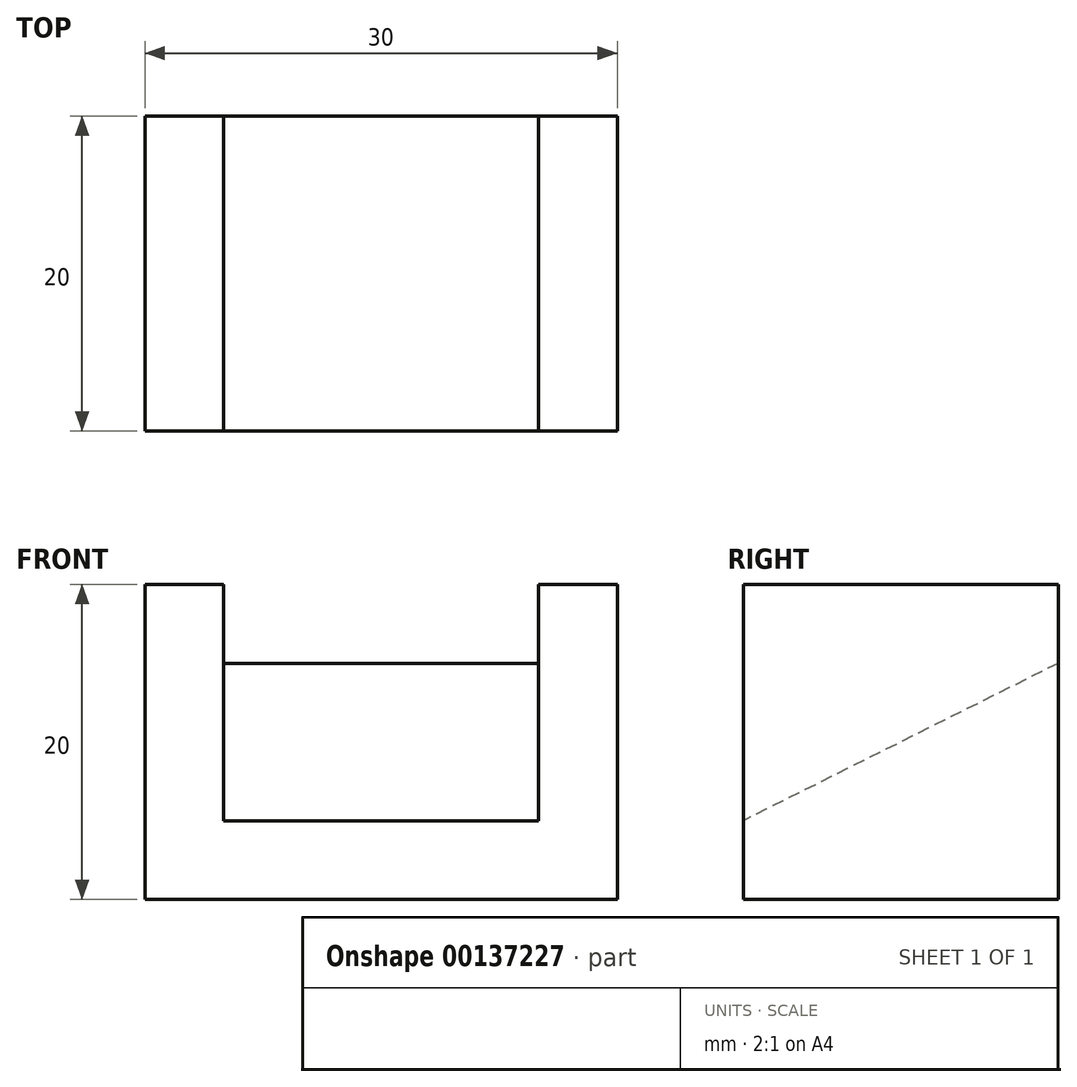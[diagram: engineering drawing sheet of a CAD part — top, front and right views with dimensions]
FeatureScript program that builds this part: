
annotation { "Feature Type Name" : "Feature", "Feature Type Description" : "" }
export const myFeature = defineFeature(function(context is Context, id is Id, definition is map)
    precondition{}
    {
        {
            var Q0;
            Q0=qCreatedBy(makeId("Front.planeOp"),FACE);
            var sketch = newSketch(context, id + "F0", { "sketchPlane" : qUnion([Q0])});
            skLineSegment(sketch, "E0", {"start": v(0, 0) * mm, "end": v(30, 0) * mm});
            skLineSegment(sketch, "E1", {"start": v(30, 0) * mm, "end": v(30, 20) * mm});
            skLineSegment(sketch, "E2", {"start": v(30, 20) * mm, "end": v(25, 20) * mm});
            skLineSegment(sketch, "E3", {"start": v(25, 20) * mm, "end": v(25, 5) * mm});
            skLineSegment(sketch, "E4", {"start": v(25, 5) * mm, "end": v(5, 5) * mm});
            skLineSegment(sketch, "E5", {"start": v(5, 5) * mm, "end": v(5, 20) * mm});
            skLineSegment(sketch, "E6", {"start": v(5, 20) * mm, "end": v(0, 20) * mm});
            skLineSegment(sketch, "E7", {"start": v(0, 20) * mm, "end": v(0, 0) * mm});
            skSolve(sketch);
        }
        {
            var Q0;
            Q0=makeQuery(id+"F0.imprint","IMPRINT",FACE,{"disambiguationData":[TD([[makeQuery(id+"F0.imprint","IMPRINT",EDGE,{"derivedFrom":sQuery(id+"F0.wireOp",EDGE,"E0")}),1.0]])]});
            extrude(context, id + "F1", {"entities" : qUnion([Q0]), "oppositeDirection" : true, "depth" : 20 * mm});
        }
        {
            var Q0;
            Q0=makeQuery(id+"F1.opExtrude","SWEPT_FACE",FACE,{"disambiguationData":[OSD([sQuery(id+"F0.wireOp",EDGE,"E5")])]});
            var sketch = newSketch(context, id + "F2", { "sketchPlane" : qUnion([Q0])});
            skLineSegment(sketch, "E8", {"start": v(20, 20) * mm, "end": v(20, 15) * mm, "construction": true});
            skLineSegment(sketch, "E9", {"start": v(20, 15) * mm, "end": v(0, 5) * mm});
            skLineSegment(sketch, "E10", {"start": v(0, 5) * mm, "end": v(20, 5) * mm});
            skLineSegment(sketch, "E11", {"start": v(20, 5) * mm, "end": v(20, 15) * mm});
            skSolve(sketch);
        }
        {
            var Q0;
            Q0=makeQuery(id+"F2.imprint","IMPRINT",FACE,{"disambiguationData":[TD([[makeQuery(id+"F2.imprint","IMPRINT",EDGE,{"derivedFrom":sQuery(id+"F2.wireOp",EDGE,"E9")}),1.0]])]});
            extrude(context, id + "F3", {"entities" : qUnion([Q0]), "operationType" : NewBodyOperationType.ADD, "depth" : 20 * mm});
        }
    });
